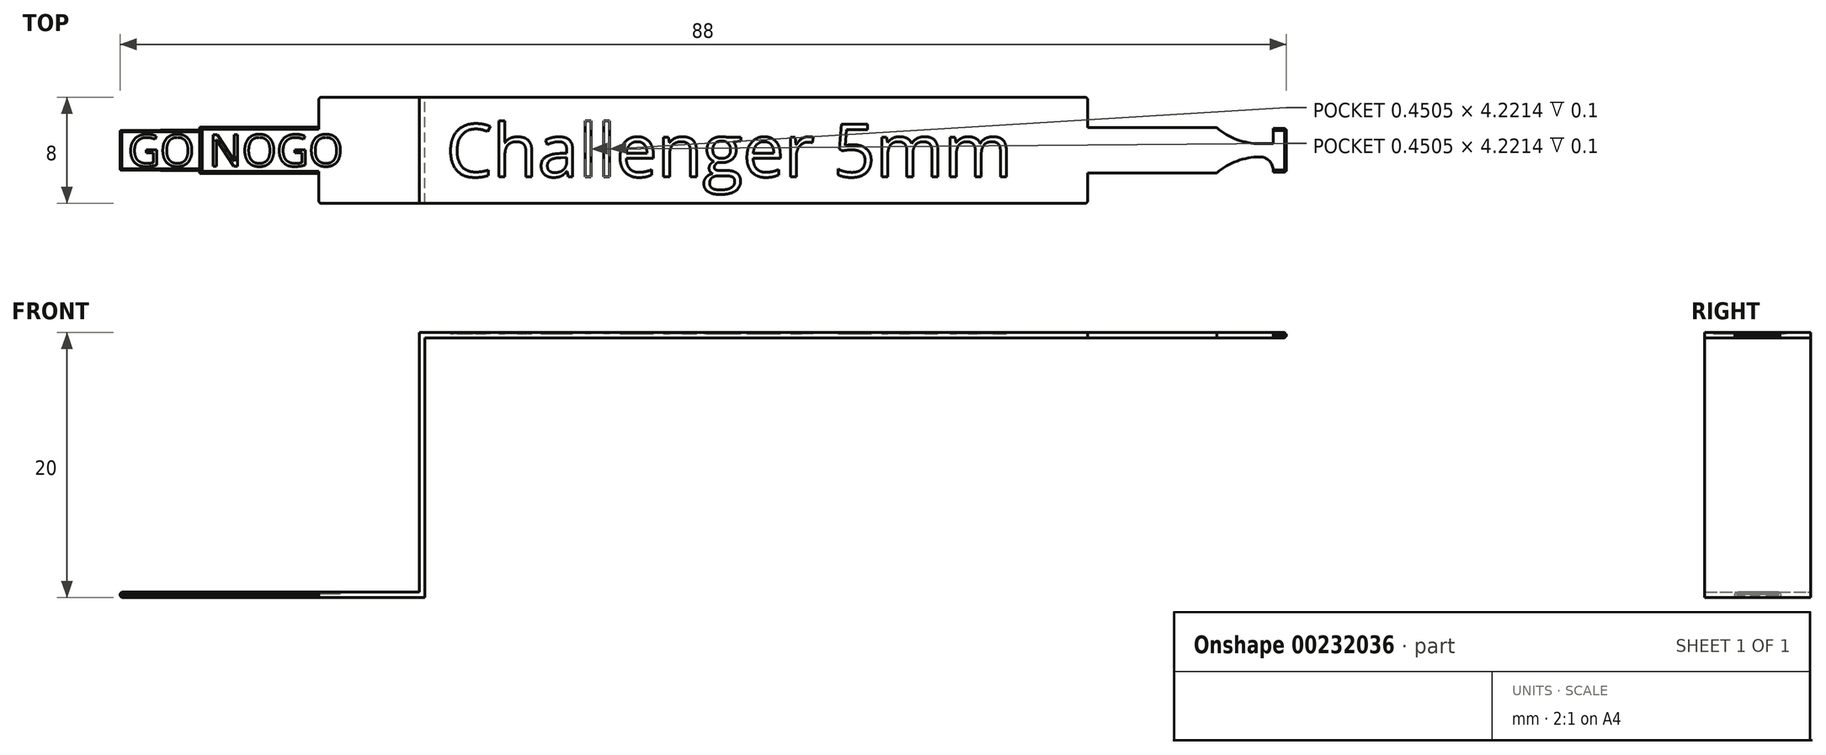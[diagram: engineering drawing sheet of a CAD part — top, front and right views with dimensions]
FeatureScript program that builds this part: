
annotation { "Feature Type Name" : "Feature", "Feature Type Description" : "" }
export const myFeature = defineFeature(function(context is Context, id is Id, definition is map)
    precondition{}
    {
        {
            var Q0;
            Q0=qCreatedBy(makeId("Front.planeOp"),FACE);
            var sketch = newSketch(context, id + "F0", { "sketchPlane" : qUnion([Q0])});
            skLineSegment(sketch, "E0", {"start": v(0, 0) * mm, "end": v(23, 0) * mm});
            skLineSegment(sketch, "E1", {"start": v(23, 0) * mm, "end": v(23, 19.6) * mm});
            skLineSegment(sketch, "E2", {"start": v(23, 19.6) * mm, "end": v(88, 19.6) * mm});
            skLineSegment(sketch, "E3", {"start": v(88, 19.6) * mm, "end": v(88, 20) * mm});
            skLineSegment(sketch, "E4", {"start": v(88, 20) * mm, "end": v(22.6, 20) * mm});
            skLineSegment(sketch, "E5", {"start": v(22.6, 20) * mm, "end": v(22.6, 0.4) * mm});
            skLineSegment(sketch, "E6", {"start": v(22.6, 0.4) * mm, "end": v(0, 0.4) * mm});
            skLineSegment(sketch, "E7", {"start": v(0, 0.4) * mm, "end": v(0, 0) * mm});
            skLineSegment(sketch, "E8", {"start": v(73, 20) * mm, "end": v(73, 19.6) * mm});
            skLineSegment(sketch, "E9", {"start": v(6, 0.4) * mm, "end": v(6, 0) * mm});
            skLineSegment(sketch, "E10", {"start": v(15, 0.4) * mm, "end": v(15, 0) * mm});
            skLineSegment(sketch, "E11", {"start": v(87, 20) * mm, "end": v(87, 19.6) * mm});
            skLineSegment(sketch, "E12", {"start": v(81, 20) * mm, "end": v(81, 19.6) * mm});
            skSolve(sketch);
        }
        {
            var Q0;
            {var subQ3=sQuery(id+"F0.wireOp",EDGE,"E1");Q0=makeQuery(id+"F0.imprint","IMPRINT",FACE,{"disambiguationData":[TD([[makeQuery(id+"F0.imprint","IMPRINT",EDGE,{"derivedFrom":subQ3}),1.0]])]});}
            extrude(context, id + "F1", {"entities" : qUnion([Q0]), "endBound" : BoundingType.SYMMETRIC, "depth" : 8 * mm});
        }
        {
            var Q0;
            {var subQ0=sQuery(id+"F0.wireOp",EDGE,"E9");Q0=makeQuery(id+"F0.imprint","IMPRINT",FACE,{"disambiguationData":[TD([[makeQuery(id+"F0.imprint","IMPRINT",EDGE,{"derivedFrom":subQ0}),1.0]])]});}
            extrude(context, id + "F2", {"entities" : qUnion([Q0]), "operationType" : NewBodyOperationType.ADD, "endBound" : BoundingType.SYMMETRIC, "depth" : 3.5 * mm});
        }
        {
            var Q0;
            {var subQ0=sQuery(id+"F0.wireOp",EDGE,"E7");Q0=makeQuery(id+"F0.imprint","IMPRINT",FACE,{"disambiguationData":[TD([[makeQuery(id+"F0.imprint","IMPRINT",EDGE,{"derivedFrom":subQ0}),1.0]])]});}
            extrude(context, id + "F3", {"entities" : qUnion([Q0]), "operationType" : NewBodyOperationType.ADD, "endBound" : BoundingType.SYMMETRIC, "depth" : 3.1 * mm});
        }
        {
            var Q0;
            {var subQ0=sQuery(id+"F0.wireOp",EDGE,"E3");Q0=makeQuery(id+"F0.imprint","IMPRINT",FACE,{"disambiguationData":[TD([[makeQuery(id+"F0.imprint","IMPRINT",EDGE,{"derivedFrom":subQ0}),1.0]])]});}
            extrude(context, id + "F4", {"entities" : qUnion([Q0]), "operationType" : NewBodyOperationType.ADD, "endBound" : BoundingType.SYMMETRIC, "depth" : 3.3 * mm});
        }
        {
            var Q0;
            {var subQ0=sQuery(id+"F0.wireOp",EDGE,"E8");Q0=makeQuery(id+"F0.imprint","IMPRINT",FACE,{"disambiguationData":[TD([[makeQuery(id+"F0.imprint","IMPRINT",EDGE,{"derivedFrom":subQ0}),1.0]])]});}
            extrude(context, id + "F5", {"entities" : qUnion([Q0]), "operationType" : NewBodyOperationType.ADD, "endBound" : BoundingType.SYMMETRIC, "depth" : 3.4 * mm});
        }
        {
            var Q0;
            {var subQ0=sQuery(id+"F0.wireOp",EDGE,"E11");Q0=makeQuery(id+"F0.imprint","IMPRINT",FACE,{"disambiguationData":[TD([[makeQuery(id+"F0.imprint","IMPRINT",EDGE,{"derivedFrom":subQ0}),-1.0]])]});}
            extrude(context, id + "F6", {"entities" : qUnion([Q0]), "operationType" : NewBodyOperationType.ADD, "endBound" : BoundingType.SYMMETRIC, "depth" : 1 * mm});
        }
        {
            var Q0;
            Q0=makeQuery(id+"F4.opExtrude","SWEPT_FACE",FACE,{"disambiguationData":[OSD([sQuery(id+"F0.wireOp",EDGE,"E4")])]});
            var sketch = newSketch(context, id + "F7", { "sketchPlane" : qUnion([Q0])});
            skArc(sketch, "E13", {"start": v(87, 1.5) * mm, "mid": v(86.7, 0.8) * mm, "end": v(86, 0.5) * mm});
            skArc(sketch, "E14", {"start": v(87, -1.5) * mm, "mid": v(86.7, -0.8) * mm, "end": v(86, -0.5) * mm});
            skLineSegment(sketch, "E15", {"start": v(86, -0.5) * mm, "end": v(87, -0.5) * mm});
            skLineSegment(sketch, "E16", {"start": v(87, -0.5) * mm, "end": v(87, -1.5) * mm});
            skLineSegment(sketch, "E17", {"start": v(86, 0.5) * mm, "end": v(87, 0.5) * mm});
            skLineSegment(sketch, "E18", {"start": v(87, 0.5) * mm, "end": v(87, 1.5) * mm});
            skSolve(sketch);
        }
        {
            var Q0;
            Q0=makeQuery(id+"F7.imprint","IMPRINT",FACE,{"disambiguationData":[TD([[makeQuery(id+"F7.imprint","IMPRINT",EDGE,{"derivedFrom":sQuery(id+"F7.wireOp",EDGE,"E13")}),1.0]])]});
            var Q1;
            Q1=makeQuery(id+"F7.imprint","IMPRINT",FACE,{"disambiguationData":[TD([[makeQuery(id+"F7.imprint","IMPRINT",EDGE,{"derivedFrom":sQuery(id+"F7.wireOp",EDGE,"E14")}),-1.0]])]});
            extrude(context, id + "F8", {"entities" : qUnion([Q0, Q1]), "operationType" : NewBodyOperationType.ADD, "oppositeDirection" : true, "depth" : 0.4 * mm});
        }
        {
            var Q0;
            Q0=makeQuery(id+"F6.opExtrude","SWEPT_FACE",FACE,{"disambiguationData":[OSD([sQuery(id+"F0.wireOp",EDGE,"E4")])]});
            var sketch = newSketch(context, id + "F9", { "sketchPlane" : qUnion([Q0])});
            skLineSegment(sketch, "E19", {"start": v(81, 1.7) * mm, "end": v(81, 0.5) * mm});
            skLineSegment(sketch, "E20", {"start": v(81, 0.5) * mm, "end": v(86, 0.5) * mm});
            skArc(sketch, "E21", {"start": v(86, 0.5) * mm, "mid": v(84.27, 0.8) * mm, "end": v(82.75, 1.7) * mm});
            skLineSegment(sketch, "E22", {"start": v(82.75, 1.7) * mm, "end": v(81, 1.7) * mm});
            skLineSegment(sketch, "E23.MirrorCS", {"start": v(81, -1.7) * mm, "end": v(81, -0.5) * mm});
            skLineSegment(sketch, "E24.MirrorCS", {"start": v(81, -0.5) * mm, "end": v(86, -0.5) * mm});
            skArc(sketch, "E25.MirrorCS", {"start": v(86, -0.5) * mm, "mid": v(84.27, -0.8) * mm, "end": v(82.75, -1.7) * mm});
            skLineSegment(sketch, "E26.MirrorCS", {"start": v(82.75, -1.7) * mm, "end": v(81, -1.7) * mm});
            skSolve(sketch);
        }
        {
            var Q0;
            Q0=makeQuery(id+"F9.imprint","IMPRINT",FACE,{"disambiguationData":[TD([[makeQuery(id+"F9.imprint","IMPRINT",EDGE,{"derivedFrom":sQuery(id+"F9.wireOp",EDGE,"E19")}),1.0]])]});
            var Q1;
            Q1=makeQuery(id+"F9.imprint","IMPRINT",FACE,{"disambiguationData":[TD([[makeQuery(id+"F9.imprint","IMPRINT",EDGE,{"derivedFrom":sQuery(id+"F9.wireOp",EDGE,"E23.MirrorCS")}),-1.0]])]});
            var Q2;
            Q2=makeQuery(id+"F9.imprint","IMPRINT",FACE,{"disambiguationData":[TD([[makeQuery(id+"F9.imprint","IMPRINT",EDGE,{"derivedFrom":sQuery(id+"F9.wireOp",EDGE,"E19")}),-1.0]])]});
            extrude(context, id + "F10", {"entities" : qUnion([Q0, Q1, Q2]), "operationType" : NewBodyOperationType.ADD, "oppositeDirection" : true, "depth" : 0.4 * mm});
        }
        {
            var Q0;
            Q0=makeQuery(id+"F4.opExtrude","SWEPT_EDGE",EDGE,{"disambiguationData":[OSD([sQuery(id+"F0.wireOp",EDGE,"E3"),sQuery(id+"F0.wireOp",EDGE,"E4")])]});
            var Q1;
            Q1=makeQuery(id+"F4.opExtrude","SWEPT_EDGE",EDGE,{"disambiguationData":[OSD([sQuery(id+"F0.wireOp",EDGE,"E2"),sQuery(id+"F0.wireOp",EDGE,"E3")])]});
            var Q2;
            Q2=makeQuery(id+"F4.opExtrude","CAP_EDGE",EDGE,{"disambiguationData":[OSD([sQuery(id+"F0.wireOp",EDGE,"E4")])],"isStart":false});
            var Q3;
            Q3=makeQuery(id+"F4.opExtrude","CAP_EDGE",EDGE,{"disambiguationData":[OSD([sQuery(id+"F0.wireOp",EDGE,"E2")])],"isStart":false});
            var Q4;
            Q4=makeQuery(id+"F4.opExtrude","CAP_EDGE",EDGE,{"disambiguationData":[OSD([sQuery(id+"F0.wireOp",EDGE,"E4")])],"isStart":true});
            var Q5;
            Q5=makeQuery(id+"F4.opExtrude","CAP_EDGE",EDGE,{"disambiguationData":[OSD([sQuery(id+"F0.wireOp",EDGE,"E2")])],"isStart":true});
            var Q6;
            Q6=makeQuery(id+"F2.opExtrude","CAP_EDGE",EDGE,{"disambiguationData":[OSD([sQuery(id+"F0.wireOp",EDGE,"E6")])],"isStart":true});
            var Q7;
            Q7=makeQuery(id+"F2.opExtrude","CAP_EDGE",EDGE,{"disambiguationData":[OSD([sQuery(id+"F0.wireOp",EDGE,"E0")])],"isStart":true});
            var Q8;
            Q8=makeQuery(id+"F2.opExtrude","CAP_EDGE",EDGE,{"disambiguationData":[OSD([sQuery(id+"F0.wireOp",EDGE,"E6")])],"isStart":false});
            var Q9;
            Q9=makeQuery(id+"F2.opExtrude","CAP_EDGE",EDGE,{"disambiguationData":[OSD([sQuery(id+"F0.wireOp",EDGE,"E0")])],"isStart":false});
            var Q10;
            Q10=makeQuery(id+"F3.opExtrude","CAP_EDGE",EDGE,{"disambiguationData":[OSD([sQuery(id+"F0.wireOp",EDGE,"E6")])],"isStart":false});
            var Q11;
            Q11=makeQuery(id+"F3.opExtrude","CAP_EDGE",EDGE,{"disambiguationData":[OSD([sQuery(id+"F0.wireOp",EDGE,"E0")])],"isStart":false});
            var Q12;
            Q12=makeQuery(id+"F3.opExtrude","SWEPT_EDGE",EDGE,{"disambiguationData":[OSD([sQuery(id+"F0.wireOp",EDGE,"E6"),sQuery(id+"F0.wireOp",EDGE,"E7")])]});
            var Q13;
            Q13=makeQuery(id+"F3.opExtrude","SWEPT_EDGE",EDGE,{"disambiguationData":[OSD([sQuery(id+"F0.wireOp",EDGE,"E0"),sQuery(id+"F0.wireOp",EDGE,"E7")])]});
            var Q14;
            Q14=makeQuery(id+"F3.opExtrude","CAP_EDGE",EDGE,{"disambiguationData":[OSD([sQuery(id+"F0.wireOp",EDGE,"E6")])],"isStart":true});
            var Q15;
            Q15=makeQuery(id+"F3.opExtrude","CAP_EDGE",EDGE,{"disambiguationData":[OSD([sQuery(id+"F0.wireOp",EDGE,"E0")])],"isStart":true});
            chamfer(context, id + "F11", {"entities" : qUnion([Q0, Q1, Q2, Q3, Q4, Q5, Q6, Q7, Q8, Q9, Q10, Q11, Q12, Q13, Q14, Q15]), "width" : 0.15 * mm, "tangentPropagation" : true});
        }
        {
            var Q0;
            Q0=makeQuery(id+"F4.opExtrude","CAP_EDGE",EDGE,{"disambiguationData":[OSD([sQuery(id+"F0.wireOp",EDGE,"E3")])],"isStart":false});
            var Q1;
            Q1=makeQuery(id+"F4.opExtrude","CAP_EDGE",EDGE,{"disambiguationData":[OSD([sQuery(id+"F0.wireOp",EDGE,"E3")])],"isStart":true});
            var Q2;
            Q2=makeQuery(id+"F1.opExtrude","CAP_EDGE",EDGE,{"disambiguationData":[OSD([sQuery(id+"F0.wireOp",EDGE,"E8")])],"isStart":false});
            var Q3;
            Q3=makeQuery(id+"F1.opExtrude","CAP_EDGE",EDGE,{"disambiguationData":[OSD([sQuery(id+"F0.wireOp",EDGE,"E8")])],"isStart":true});
            var Q4;
            Q4=makeQuery(id+"F1.opExtrude","CAP_EDGE",EDGE,{"disambiguationData":[OSD([sQuery(id+"F0.wireOp",EDGE,"E10")])],"isStart":true});
            var Q5;
            Q5=makeQuery(id+"F1.opExtrude","CAP_EDGE",EDGE,{"disambiguationData":[OSD([sQuery(id+"F0.wireOp",EDGE,"E10")])],"isStart":false});
            var Q6;
            Q6=makeQuery(id+"F3.opExtrude","CAP_EDGE",EDGE,{"disambiguationData":[OSD([sQuery(id+"F0.wireOp",EDGE,"E7")])],"isStart":true});
            var Q7;
            Q7=makeQuery(id+"F3.opExtrude","CAP_EDGE",EDGE,{"disambiguationData":[OSD([sQuery(id+"F0.wireOp",EDGE,"E7")])],"isStart":false});
            fillet(context, id + "F12", {"entities" : qUnion([Q0, Q1, Q2, Q3, Q4, Q5, Q6, Q7]), "radius" : 0.2 * mm, "tangentPropagation" : true, "allowEdgeOverflow" : false});
        }
        {
            var Q0;
            {var subQ0=sQuery(id+"F0.wireOp",EDGE,"E6");Q0=makeQuery(id+"F3.boolean.opBoolean","MERGE",FACE,{"derivedFrom":[makeQuery(id+"F2.opExtrude","SWEPT_FACE",FACE,{"disambiguationData":[OSD([subQ0])]}),makeQuery(id+"F3.opExtrude","SWEPT_FACE",FACE,{"disambiguationData":[OSD([subQ0])]})]});}
            var sketch = newSketch(context, id + "F13", { "sketchPlane" : qUnion([Q0])});
            skText(sketch, "E27", { "text": "GO\n", "fontName": "OpenSans-Regular.ttf"});
            skText(sketch, "E28", { "text": "NOGO", "fontName": "OpenSans-Regular.ttf"});
            skLineSegment(sketch, "E29", {"start": v(6, -1.55) * mm, "end": v(6, 1.55) * mm});
            skLineSegment(sketch, "E30", {"start": v(6, 1.55) * mm, "end": v(6, 1.7) * mm});
            skLineSegment(sketch, "E31", {"start": v(6, 1.7) * mm, "end": v(6.2, 1.7) * mm});
            skLineSegment(sketch, "E32", {"start": v(6.2, 1.7) * mm, "end": v(6.2, -1.7) * mm});
            skLineSegment(sketch, "E33", {"start": v(6.2, -1.7) * mm, "end": v(6, -1.7) * mm});
            skLineSegment(sketch, "E34", {"start": v(6, -1.7) * mm, "end": v(6, -1.55) * mm});
            const initialGuessF13  = {"E27": [0.0006, -0.0012, 1, 0, 0.0024], "E28": [0.0067, -0.0012, 1, 0, 0.0024]};
            skSetInitialGuess(sketch, initialGuessF13);
            skSolve(sketch);
        }
        {
            var Q0;
            Q0=makeQuery(id+"F13.imprint","IMPRINT",FACE,{"disambiguationData":[TD([[makeQuery(id+"F13.imprint","IMPRINT",EDGE,{"derivedFrom":sQuery(id+"F13.wireOp",EDGE,"E27.sketch_text.stroke-0")}),-1.0]])]});
            var Q1;
            Q1=makeQuery(id+"F13.imprint","IMPRINT",FACE,{"disambiguationData":[TD([[makeQuery(id+"F13.imprint","IMPRINT",EDGE,{"derivedFrom":sQuery(id+"F13.wireOp",EDGE,"E27.sketch_text.stroke-20")}),-1.0]])]});
            var Q2;
            Q2=makeQuery(id+"F13.imprint","IMPRINT",FACE,{"disambiguationData":[TD([[makeQuery(id+"F13.imprint","IMPRINT",EDGE,{"derivedFrom":sQuery(id+"F13.wireOp",EDGE,"rMfZ6Xua-cZCE-byg8-JFjS-xGA2Sr2XlBS0")}),1.0]])]});
            var Q3;
            Q3=makeQuery(id+"F13.imprint","IMPRINT",FACE,{"disambiguationData":[TD([[makeQuery(id+"F13.imprint","IMPRINT",EDGE,{"derivedFrom":sQuery(id+"F13.wireOp",EDGE,"E28.sketch_text.stroke-0")}),-1.0]])]});
            var Q4;
            Q4=makeQuery(id+"F13.imprint","IMPRINT",FACE,{"disambiguationData":[TD([[makeQuery(id+"F13.imprint","IMPRINT",EDGE,{"derivedFrom":sQuery(id+"F13.wireOp",EDGE,"E28.sketch_text.stroke-15")}),-1.0]])]});
            var Q5;
            Q5=makeQuery(id+"F13.imprint","IMPRINT",FACE,{"disambiguationData":[TD([[makeQuery(id+"F13.imprint","IMPRINT",EDGE,{"derivedFrom":sQuery(id+"F13.wireOp",EDGE,"E28.sketch_text.stroke-31")}),-1.0]])]});
            var Q6;
            {var subQ1=sQuery(id+"F13.wireOp",EDGE,"E28.sketch_text.stroke-54");Q6=makeQuery(id+"F13.imprint","IMPRINT",FACE,{"disambiguationData":[TD([[makeQuery(id+"F13.imprint","IMPRINT",EDGE,{"derivedFrom":subQ1}),-1.0]])]});}
            var Q7;
            {var subQ0=sQuery(id+"F13.wireOp",EDGE,"E29");var subQ1=sQuery(id+"F0.wireOp",EDGE,"E6");var subQ2=makeQuery(id+"F3.boolean.opBoolean","MERGE",FACE,{"derivedFrom":[makeQuery(id+"F2.boolean.opBoolean","MERGE",FACE,{"derivedFrom":[makeQuery(id+"F1.opExtrude","SWEPT_FACE",FACE,{"disambiguationData":[OSD([subQ1])]}),makeQuery(id+"F2.opExtrude","SWEPT_FACE",FACE,{"disambiguationData":[OSD([subQ1])]})]}),makeQuery(id+"F3.opExtrude","SWEPT_FACE",FACE,{"disambiguationData":[OSD([subQ1])]})]});var subQ5=makeQuery(id+"F13.imprint","INTERSECT",VERTEX,{"derivedFrom":[makeQuery(id+"F11.opChamfer","BLEND_EDGE",EDGE,{"blendedFrom":[makeQuery(id+"F3.opExtrude","CAP_EDGE",EDGE,{"disambiguationData":[OSD([subQ1])],"isStart":true}),subQ2],"blendedInto":[subQ2]}),subQ0]});var subQ11=makeQuery(id+"F13.imprint","INTERSECT",VERTEX,{"derivedFrom":[makeQuery(id+"F11.opChamfer","BLEND_EDGE",EDGE,{"blendedFrom":[makeQuery(id+"F3.opExtrude","CAP_EDGE",EDGE,{"disambiguationData":[OSD([subQ1])],"isStart":false}),subQ2],"blendedInto":[subQ2]}),subQ0]});Q7=makeQuery(id+"F13.imprint","IMPRINT",FACE,{"disambiguationData":[TD([[makeQuery(id+"F13.imprint","IMPRINT",EDGE,{"disambiguationData":[TD([[subQ5,1.0],[subQ11,-1.0]])],"derivedFrom":subQ0}),-1.0]])]});}
            extrude(context, id + "F14", {"entities" : qUnion([Q0, Q1, Q2, Q3, Q4, Q5, Q6, Q7]), "operationType" : NewBodyOperationType.REMOVE, "oppositeDirection" : true, "depth" : 0.1 * mm});
        }
        {
            var Q0;
            {var subQ0=sQuery(id+"F0.wireOp",EDGE,"E4");Q0=makeQuery(id+"F5.boolean.opBoolean","MERGE",FACE,{"derivedFrom":[makeQuery(id+"F1.opExtrude","SWEPT_FACE",FACE,{"disambiguationData":[OSD([subQ0])]}),makeQuery(id+"F5.opExtrude","SWEPT_FACE",FACE,{"disambiguationData":[OSD([subQ0])]})]});}
            var sketch = newSketch(context, id + "F15", { "sketchPlane" : qUnion([Q0])});
            skText(sketch, "E35", { "text": "Challenger 5mm", "fontName": "OpenSans-Regular.ttf"});
            const initialGuessF15  = {"E35": [0.0246, -0.002, 1, 0, 0.004]};
            skSetInitialGuess(sketch, initialGuessF15);
            skSolve(sketch);
        }
        {
            var Q0;
            Q0=makeQuery(id+"F15.imprint","IMPRINT",FACE,{"disambiguationData":[TD([[makeQuery(id+"F15.imprint","IMPRINT",EDGE,{"derivedFrom":sQuery(id+"F15.wireOp",EDGE,"E35.sketch_text.stroke-0")}),-1.0]])]});
            var Q1;
            Q1=makeQuery(id+"F15.imprint","IMPRINT",FACE,{"disambiguationData":[TD([[makeQuery(id+"F15.imprint","IMPRINT",EDGE,{"derivedFrom":sQuery(id+"F15.wireOp",EDGE,"E35.sketch_text.stroke-15")}),-1.0]])]});
            var Q2;
            Q2=makeQuery(id+"F15.imprint","IMPRINT",FACE,{"disambiguationData":[TD([[makeQuery(id+"F15.imprint","IMPRINT",EDGE,{"derivedFrom":sQuery(id+"F15.wireOp",EDGE,"E35.sketch_text.stroke-33")}),-1.0]])]});
            var Q3;
            Q3=makeQuery(id+"F15.imprint","IMPRINT",FACE,{"disambiguationData":[TD([[makeQuery(id+"F15.imprint","IMPRINT",EDGE,{"derivedFrom":sQuery(id+"F15.wireOp",EDGE,"E35.sketch_text.stroke-60")}),-1.0]])]});
            var Q4;
            Q4=makeQuery(id+"F15.imprint","IMPRINT",FACE,{"disambiguationData":[TD([[makeQuery(id+"F15.imprint","IMPRINT",EDGE,{"derivedFrom":sQuery(id+"F15.wireOp",EDGE,"E35.sketch_text.stroke-64")}),-1.0]])]});
            var Q5;
            Q5=makeQuery(id+"F15.imprint","IMPRINT",FACE,{"disambiguationData":[TD([[makeQuery(id+"F15.imprint","IMPRINT",EDGE,{"derivedFrom":sQuery(id+"F15.wireOp",EDGE,"E35.sketch_text.stroke-68")}),-1.0]])]});
            var Q6;
            Q6=makeQuery(id+"F15.imprint","IMPRINT",FACE,{"disambiguationData":[TD([[makeQuery(id+"F15.imprint","IMPRINT",EDGE,{"derivedFrom":sQuery(id+"F15.wireOp",EDGE,"E35.sketch_text.stroke-87")}),-1.0]])]});
            var Q7;
            Q7=makeQuery(id+"F15.imprint","IMPRINT",FACE,{"disambiguationData":[TD([[makeQuery(id+"F15.imprint","IMPRINT",EDGE,{"derivedFrom":sQuery(id+"F15.wireOp",EDGE,"E35.sketch_text.stroke-104")}),-1.0]])]});
            var Q8;
            Q8=makeQuery(id+"F15.imprint","IMPRINT",FACE,{"disambiguationData":[TD([[makeQuery(id+"F15.imprint","IMPRINT",EDGE,{"derivedFrom":sQuery(id+"F15.wireOp",EDGE,"E35.sketch_text.stroke-148")}),-1.0]])]});
            var Q9;
            Q9=makeQuery(id+"F15.imprint","IMPRINT",FACE,{"disambiguationData":[TD([[makeQuery(id+"F15.imprint","IMPRINT",EDGE,{"derivedFrom":sQuery(id+"F15.wireOp",EDGE,"E35.sketch_text.stroke-167")}),-1.0]])]});
            var Q10;
            Q10=makeQuery(id+"F15.imprint","IMPRINT",FACE,{"disambiguationData":[TD([[makeQuery(id+"F15.imprint","IMPRINT",EDGE,{"derivedFrom":sQuery(id+"F15.wireOp",EDGE,"E35.sketch_text.stroke-180")}),-1.0]])]});
            var Q11;
            Q11=makeQuery(id+"F15.imprint","IMPRINT",FACE,{"disambiguationData":[TD([[makeQuery(id+"F15.imprint","IMPRINT",EDGE,{"derivedFrom":sQuery(id+"F15.wireOp",EDGE,"E35.sketch_text.stroke-199")}),-1.0]])]});
            var Q12;
            Q12=makeQuery(id+"F15.imprint","IMPRINT",FACE,{"disambiguationData":[TD([[makeQuery(id+"F15.imprint","IMPRINT",EDGE,{"derivedFrom":sQuery(id+"F15.wireOp",EDGE,"E35.sketch_text.stroke-227")}),-1.0]])]});
            extrude(context, id + "F16", {"entities" : qUnion([Q0, Q1, Q2, Q3, Q4, Q5, Q6, Q7, Q8, Q9, Q10, Q11, Q12]), "operationType" : NewBodyOperationType.REMOVE, "oppositeDirection" : true, "depth" : 0.1 * mm});
        }
        {
            var Q0;
            Q0=makeQuery(id+"F9.imprint","IMPRINT",FACE,{"disambiguationData":[TD([[makeQuery(id+"F9.imprint","IMPRINT",EDGE,{"derivedFrom":sQuery(id+"F9.wireOp",EDGE,"E19")}),-1.0]])]});
            extrude(context, id + "F17", {"entities" : qUnion([Q0]), "operationType" : NewBodyOperationType.ADD, "oppositeDirection" : true, "depth" : 0.4 * mm});
        }
        {
            var Q0;
            Q0=qCreatedBy(makeId("Top.planeOp"),FACE);
            var sketch = newSketch(context, id + "F18", { "sketchPlane" : qUnion([Q0])});
            skLineSegment(sketch, "E36", {"start": v(0, 0) * mm, "end": v(0, -1.5) * mm});
            skLineSegment(sketch, "E37", {"start": v(0, -1.5) * mm, "end": v(6, -1.5) * mm});
            skLineSegment(sketch, "E38", {"start": v(6, -1.5) * mm, "end": v(6, -1.55) * mm});
            skLineSegment(sketch, "E39", {"start": v(6, -1.55) * mm, "end": v(0, -1.5) * mm});
            skLineSegment(sketch, "E40", {"start": v(0, 0) * mm, "end": v(0, 1.5) * mm});
            skLineSegment(sketch, "E41", {"start": v(0, 1.5) * mm, "end": v(6, 1.5) * mm});
            skLineSegment(sketch, "E42", {"start": v(6, 1.5) * mm, "end": v(6, 1.55) * mm});
            skLineSegment(sketch, "E43", {"start": v(6, 1.55) * mm, "end": v(0, 1.5) * mm});
            skLineSegment(sketch, "E44", {"start": v(0, -1.5) * mm, "end": v(0, -1.55) * mm});
            skLineSegment(sketch, "E45", {"start": v(0, -1.55) * mm, "end": v(6, -1.55) * mm});
            skLineSegment(sketch, "E46", {"start": v(0, 1.5) * mm, "end": v(0, 1.55) * mm});
            skLineSegment(sketch, "E47", {"start": v(0, 1.55) * mm, "end": v(6, 1.55) * mm});
            skSolve(sketch);
        }
        {
            var Q0;
            Q0=makeQuery(id+"F18.imprint","IMPRINT",FACE,{"disambiguationData":[TD([[makeQuery(id+"F18.imprint","IMPRINT",EDGE,{"derivedFrom":sQuery(id+"F18.wireOp",EDGE,"E39")}),1.0]])]});
            var Q1;
            Q1=makeQuery(id+"F18.imprint","IMPRINT",FACE,{"disambiguationData":[TD([[makeQuery(id+"F18.imprint","IMPRINT",EDGE,{"derivedFrom":sQuery(id+"F18.wireOp",EDGE,"E43")}),-1.0]])]});
            extrude(context, id + "F19", {"entities" : qUnion([Q0, Q1]), "operationType" : NewBodyOperationType.REMOVE, "depth" : 25 * mm});
        }
    });
